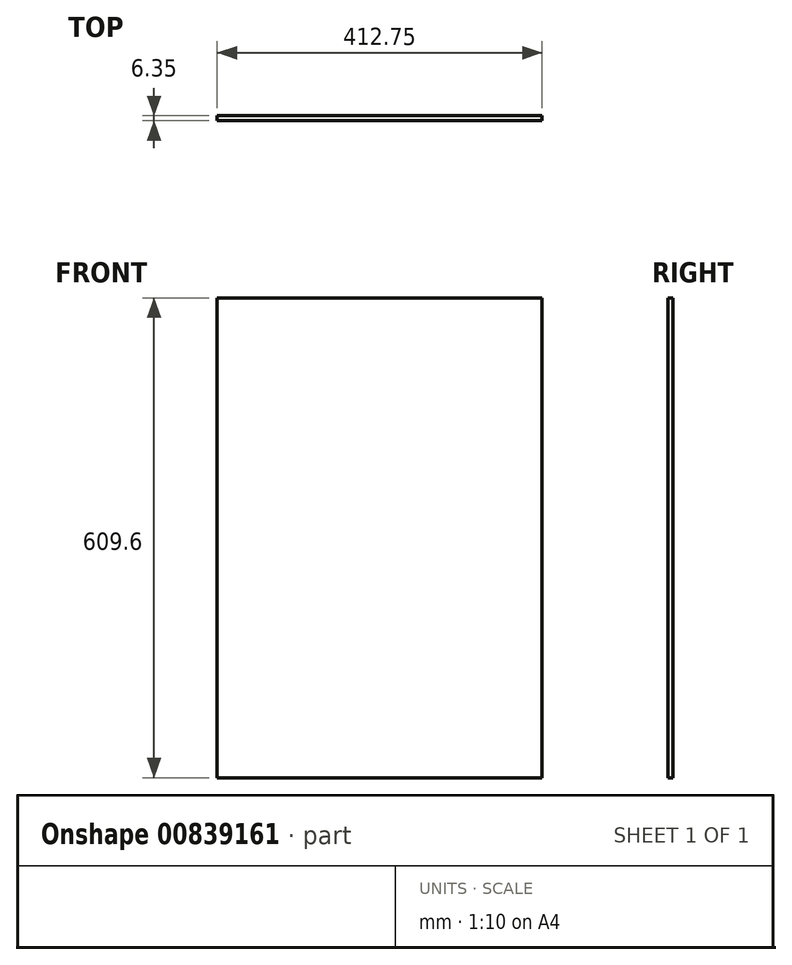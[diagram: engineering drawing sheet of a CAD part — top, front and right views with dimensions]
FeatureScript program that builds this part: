
annotation { "Feature Type Name" : "Feature", "Feature Type Description" : "" }
export const myFeature = defineFeature(function(context is Context, id is Id, definition is map)
    precondition{}
    {
        {
            var Q0;
            Q0=qCreatedBy(makeId("Front.planeOp"),FACE);
            var sketch = newSketch(context, id + "F0", { "sketchPlane" : qUnion([Q0])});
            skLineSegment(sketch, "E0.bottom", {"start": v(0, 0) * mm, "end": v(-412.75, 0) * mm});
            skLineSegment(sketch, "E0.top", {"start": v(0, 609.6) * mm, "end": v(-412.75, 609.6) * mm});
            skLineSegment(sketch, "E0.left", {"start": v(0, 0) * mm, "end": v(0, 609.6) * mm});
            skLineSegment(sketch, "E0.right", {"start": v(-412.75, 0) * mm, "end": v(-412.75, 609.6) * mm});
            skSolve(sketch);
        }
        {
            var Q0;
            Q0 = qSketchRegion(id + "F0", true);
            extrude(context, id + "F1", {"entities" : qUnion([Q0]), "oppositeDirection" : true, "depth" : 6.35 * mm, "offsetDistance" : 25.4 * mm});
        }
    });
